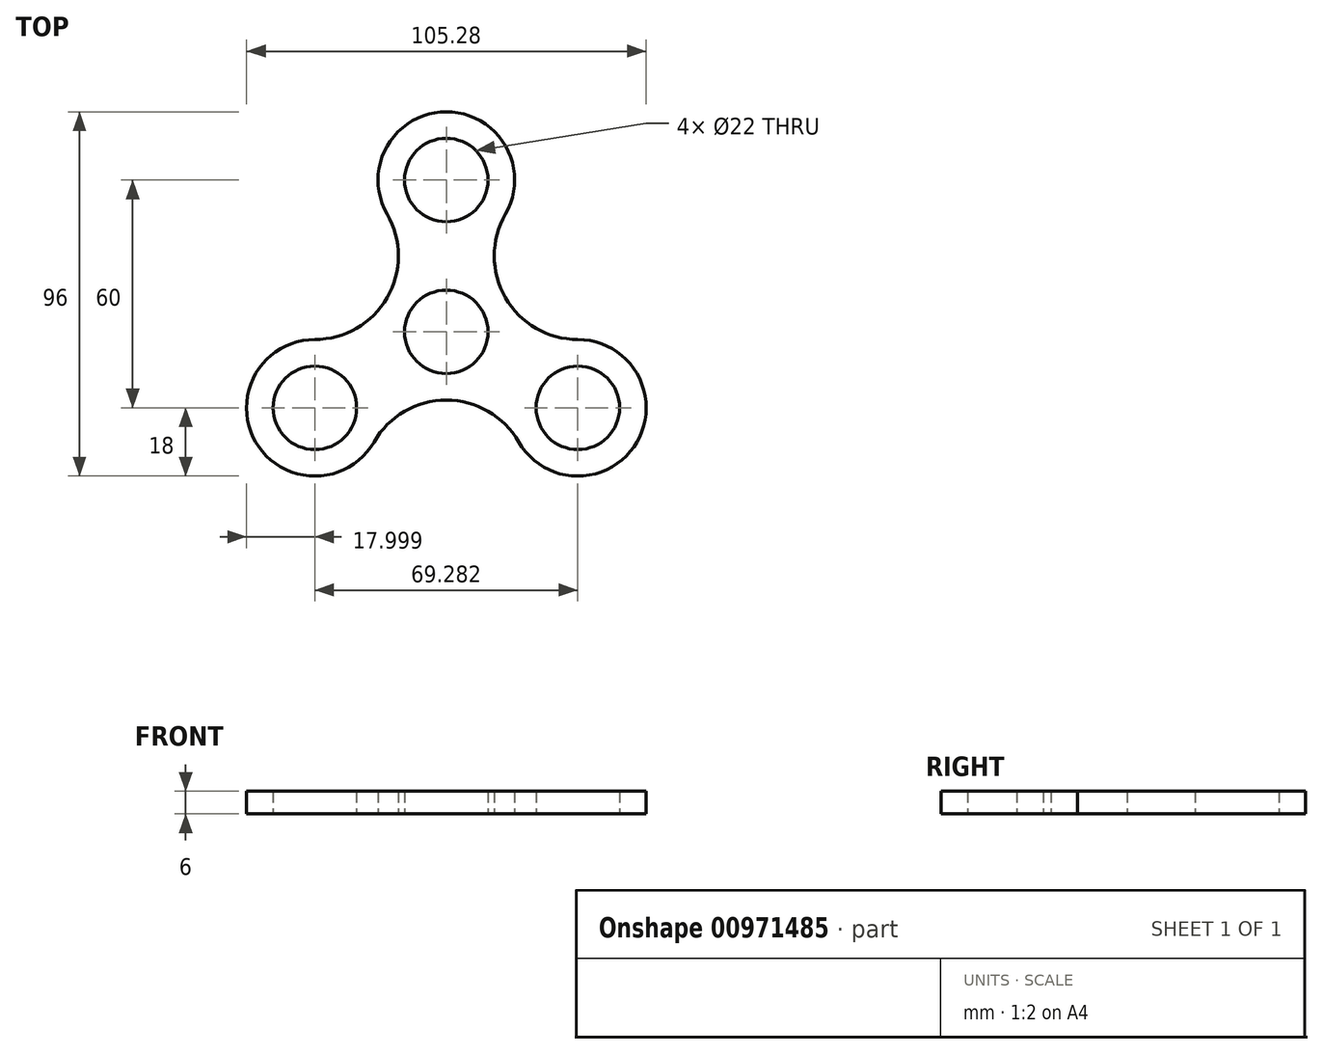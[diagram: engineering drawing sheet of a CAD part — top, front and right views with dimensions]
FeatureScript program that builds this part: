
annotation { "Feature Type Name" : "Feature", "Feature Type Description" : "" }
export const myFeature = defineFeature(function(context is Context, id is Id, definition is map)
    precondition{}
    {
        {
            var Q0;
            Q0=qCreatedBy(makeId("Top.planeOp"),FACE);
            var sketch = newSketch(context, id + "F0", { "sketchPlane" : qUnion([Q0])});
            skCircle(sketch, "E0", {"center": v(0, 0) * mm, "radius": 11 * mm});
            skCircle(sketch, "E1", {"center": v(0, 40) * mm, "radius": 11 * mm});
            skCircle(sketch, "E2.1.0", {"center": v(-34.64, -20) * mm, "radius": 11 * mm});
            skCircle(sketch, "E2.2.0", {"center": v(34.64, -20) * mm, "radius": 11 * mm});
            skCircle(sketch, "E3.0", {"center": v(0, 40) * mm, "radius": 18 * mm});
            skCircle(sketch, "E4.0", {"center": v(0, 0) * mm, "radius": 18 * mm});
            skCircle(sketch, "E5.0", {"center": v(-34.64, -20) * mm, "radius": 18 * mm});
            skCircle(sketch, "E6.0", {"center": v(34.64, -20) * mm, "radius": 18 * mm});
            skArc(sketch, "E7", {"start": v(19.05, -29) * mm, "mid": v(0, -18) * mm, "end": v(-19.05, -29) * mm});
            skArc(sketch, "E8.1.0", {"start": v(15.59, 31) * mm, "mid": v(15.59, 9) * mm, "end": v(34.64, -2) * mm});
            skArc(sketch, "E8.2.0", {"start": v(-34.64, -2) * mm, "mid": v(-15.59, 9) * mm, "end": v(-15.59, 31) * mm});
            skSolve(sketch);
        }
        {
            var Q0;
            Q0=makeQuery(id+"F0.imprint","IMPRINT",FACE,{"disambiguationData":[TD([[makeQuery(id+"F0.imprint","IMPRINT",EDGE,{"derivedFrom":sQuery(id+"F0.wireOp",EDGE,"E2.1.0")}),-1.0]])]});
            var Q1;
            {var subQ0=sQuery(id+"F0.wireOp",EDGE,"E8.2.0");var subQ1=sQuery(id+"F0.wireOp",EDGE,"E4.0");var subQ2=makeQuery(id+"F0.imprint","INTERSECT",VERTEX,{"derivedFrom":[subQ1,subQ0]});Q1=makeQuery(id+"F0.imprint","IMPRINT",FACE,{"disambiguationData":[TD([[makeQuery(id+"F0.imprint","IMPRINT",EDGE,{"disambiguationData":[TD([[subQ2,-1.0]])],"derivedFrom":subQ1}),-1.0]])]});}
            var Q2;
            {var subQ0=sQuery(id+"F0.wireOp",EDGE,"E8.1.0");var subQ1=sQuery(id+"F0.wireOp",EDGE,"E3.0");var subQ2=makeQuery(id+"F0.imprint","INTERSECT",VERTEX,{"derivedFrom":[subQ1,subQ0]});Q2=makeQuery(id+"F0.imprint","IMPRINT",FACE,{"disambiguationData":[TD([[makeQuery(id+"F0.imprint","IMPRINT",EDGE,{"disambiguationData":[TD([[subQ2,1.0]])],"derivedFrom":subQ1}),-1.0]])]});}
            var Q3;
            Q3=makeQuery(id+"F0.imprint","IMPRINT",FACE,{"disambiguationData":[TD([[makeQuery(id+"F0.imprint","IMPRINT",EDGE,{"derivedFrom":sQuery(id+"F0.wireOp",EDGE,"E1")}),-1.0]])]});
            var Q4;
            Q4=makeQuery(id+"F0.imprint","IMPRINT",FACE,{"disambiguationData":[TD([[makeQuery(id+"F0.imprint","IMPRINT",EDGE,{"derivedFrom":sQuery(id+"F0.wireOp",EDGE,"E2.2.0")}),-1.0]])]});
            var Q5;
            {var subQ0=sQuery(id+"F0.wireOp",EDGE,"E8.1.0");var subQ1=sQuery(id+"F0.wireOp",EDGE,"E4.0");var subQ2=makeQuery(id+"F0.imprint","INTERSECT",VERTEX,{"derivedFrom":[subQ1,subQ0]});Q5=makeQuery(id+"F0.imprint","IMPRINT",FACE,{"disambiguationData":[TD([[makeQuery(id+"F0.imprint","IMPRINT",EDGE,{"disambiguationData":[TD([[subQ2,1.0]])],"derivedFrom":subQ1}),-1.0]])]});}
            var Q6;
            Q6=makeQuery(id+"F0.imprint","IMPRINT",FACE,{"disambiguationData":[TD([[makeQuery(id+"F0.imprint","IMPRINT",EDGE,{"derivedFrom":sQuery(id+"F0.wireOp",EDGE,"E0")}),-1.0]])]});
            extrude(context, id + "F1", {"entities" : qUnion([Q0, Q1, Q2, Q3, Q4, Q5, Q6]), "depth" : 6 * mm, "offsetDistance" : 25 * mm});
        }
    });
